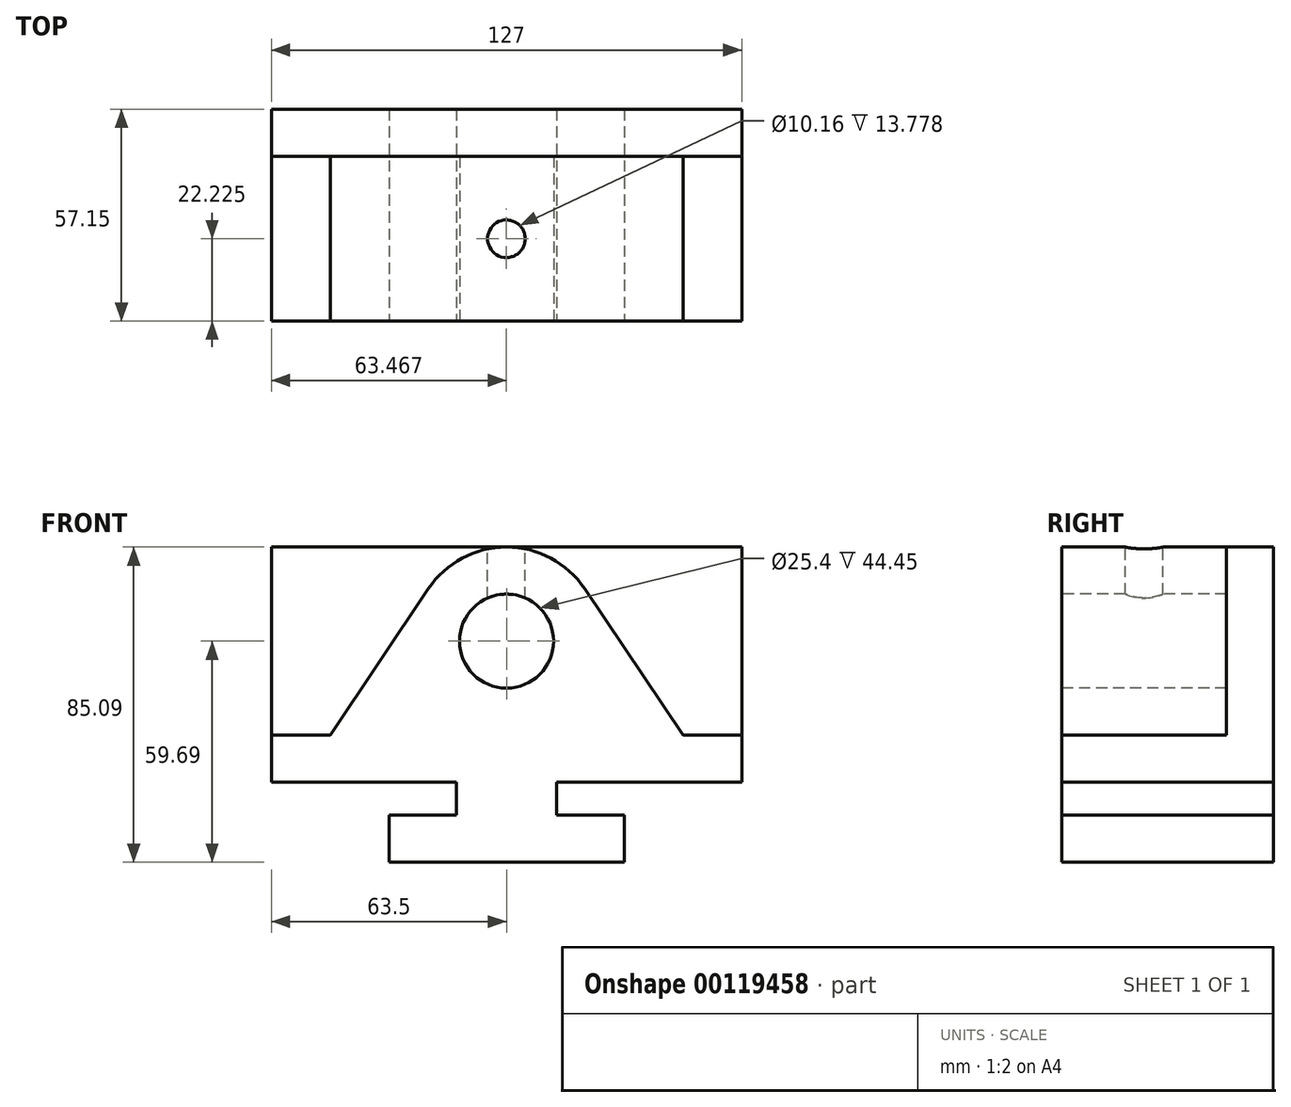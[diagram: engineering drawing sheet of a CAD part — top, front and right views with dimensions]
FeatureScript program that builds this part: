
annotation { "Feature Type Name" : "Feature", "Feature Type Description" : "" }
export const myFeature = defineFeature(function(context is Context, id is Id, definition is map)
    precondition{}
    {
        {
            var Q0;
            Q0=qCreatedBy(makeId("Front.planeOp"),FACE);
            var sketch = newSketch(context, id + "F0", { "sketchPlane" : qUnion([Q0])});
            skPoint(sketch, "E0.middle", {"position": v(0, 0) * mm});
            skLineSegment(sketch, "E1.bottom", {"start": v(31.75, 0) * mm, "end": v(-31.75, 0) * mm});
            skLineSegment(sketch, "E2", {"start": v(-13.47, 12.7) * mm, "end": v(-13.47, 21.6) * mm});
            skLineSegment(sketch, "E3", {"start": v(-13.47, 21.6) * mm, "end": v(-63.5, 21.59) * mm});
            skLineSegment(sketch, "E4", {"start": v(-63.5, 21.59) * mm, "end": v(-63.5, 85.1) * mm});
            skLineSegment(sketch, "E5", {"start": v(-63.5, 85.1) * mm, "end": v(63.5, 85.1) * mm});
            skLineSegment(sketch, "E6", {"start": v(63.5, 85.1) * mm, "end": v(63.5, 21.6) * mm});
            skLineSegment(sketch, "E7", {"start": v(-31.75, 0) * mm, "end": v(-31.75, 12.7) * mm});
            skLineSegment(sketch, "E8", {"start": v(-31.75, 12.7) * mm, "end": v(-13.47, 12.7) * mm});
            skLineSegment(sketch, "E9", {"start": v(0, 28.13) * mm, "end": v(0, -9.7) * mm, "construction": true});
            skLineSegment(sketch, "E10.MirrorCS", {"start": v(13.47, 12.7) * mm, "end": v(13.47, 21.6) * mm});
            skLineSegment(sketch, "E11.MirrorCS", {"start": v(31.75, 12.7) * mm, "end": v(13.47, 12.7) * mm});
            skLineSegment(sketch, "E12.MirrorCS", {"start": v(31.75, 0) * mm, "end": v(31.75, 12.7) * mm});
            skLineSegment(sketch, "E13.MirrorCS", {"start": v(13.47, 21.6) * mm, "end": v(63.5, 21.59) * mm});
            skSolve(sketch);
        }
        {
            var Q0;
            Q0=makeQuery(id+"F0.imprint","IMPRINT",FACE,{"disambiguationData":[TD([[makeQuery(id+"F0.imprint","IMPRINT",EDGE,{"derivedFrom":sQuery(id+"F0.wireOp",EDGE,"E1.bottom")}),-1.0]])]});
            extrude(context, id + "F1", {"entities" : qUnion([Q0]), "oppositeDirection" : true, "depth" : 57.15 * mm});
        }
        {
            var Q0;
            Q0=makeQuery(id+"F1.opExtrude","CAP_FACE",FACE,{"disambiguationData":[OSD([sQuery(id+"F0.wireOp",EDGE,"E1.bottom"),sQuery(id+"F0.wireOp",EDGE,"E2"),sQuery(id+"F0.wireOp",EDGE,"E3"),sQuery(id+"F0.wireOp",EDGE,"E4"),sQuery(id+"F0.wireOp",EDGE,"E5"),sQuery(id+"F0.wireOp",EDGE,"E6"),sQuery(id+"F0.wireOp",EDGE,"E7"),sQuery(id+"F0.wireOp",EDGE,"E8"),sQuery(id+"F0.wireOp",EDGE,"E10.MirrorCS"),sQuery(id+"F0.wireOp",EDGE,"E11.MirrorCS"),sQuery(id+"F0.wireOp",EDGE,"E12.MirrorCS"),sQuery(id+"F0.wireOp",EDGE,"E13.MirrorCS")])],"isStart":true});
            var sketch = newSketch(context, id + "F2", { "sketchPlane" : qUnion([Q0])});
            skLineSegment(sketch, "E14", {"start": v(-63.5, 85.1) * mm, "end": v(63.5, 85.1) * mm});
            skLineSegment(sketch, "E15", {"start": v(63.5, 85.1) * mm, "end": v(63.5, 34.3) * mm});
            skLineSegment(sketch, "E16", {"start": v(63.5, 34.3) * mm, "end": v(47.63, 34.3) * mm});
            skLineSegment(sketch, "E17", {"start": v(0, 0) * mm, "end": v(0, 22.1) * mm, "construction": true});
            skLineSegment(sketch, "E18.MirrorCS", {"start": v(-63.5, 34.3) * mm, "end": v(-47.63, 34.3) * mm});
            skLineSegment(sketch, "E19.MirrorCS", {"start": v(-63.5, 85.1) * mm, "end": v(-63.5, 34.3) * mm});
            skCircle(sketch, "E20", {"center": v(0, 59.7) * mm, "radius": 12.7 * mm});
            skLineSegment(sketch, "E21", {"start": v(-47.62, 34.3) * mm, "end": v(-21.1, 73.84) * mm});
            skLineSegment(sketch, "E22.MirrorCS", {"start": v(47.62, 34.3) * mm, "end": v(21.1, 73.84) * mm});
            skArc(sketch, "E23", {"start": v(-21.1, 73.84) * mm, "mid": v(0, 85.1) * mm, "end": v(21.1, 73.84) * mm});
            skSolve(sketch);
        }
        {
            var Q0;
            Q0=makeQuery(id+"F2.imprint","IMPRINT",FACE,{"disambiguationData":[TD([[makeQuery(id+"F2.imprint","IMPRINT",EDGE,{"derivedFrom":sQuery(id+"F2.wireOp",EDGE,"E18.MirrorCS")}),1.0]])]});
            var Q1;
            Q1=makeQuery(id+"F2.imprint","IMPRINT",FACE,{"disambiguationData":[TD([[makeQuery(id+"F2.imprint","IMPRINT",EDGE,{"derivedFrom":sQuery(id+"F2.wireOp",EDGE,"E20")}),1.0]])]});
            var Q2;
            {var subQ1=sQuery(id+"F2.wireOp",EDGE,"E15");Q2=makeQuery(id+"F2.imprint","IMPRINT",FACE,{"disambiguationData":[TD([[makeQuery(id+"F2.imprint","IMPRINT",EDGE,{"derivedFrom":subQ1}),-1.0]])]});}
            extrude(context, id + "F3", {"entities" : qUnion([Q0, Q1, Q2]), "operationType" : NewBodyOperationType.REMOVE, "oppositeDirection" : true, "depth" : 44.45 * mm});
        }
        {
            var Q0;
            Q0=makeQuery(id+"F1.opExtrude","SWEPT_FACE",FACE,{"disambiguationData":[OSD([sQuery(id+"F0.wireOp",EDGE,"E5")])]});
            var sketch = newSketch(context, id + "F4", { "sketchPlane" : qUnion([Q0])});
            skCircle(sketch, "E24", {"center": v(-0.03, 22.23) * mm, "radius": 5.08 * mm});
            skSolve(sketch);
        }
        {
            var Q0;
            Q0 = qSketchRegion(id + "F4", true);
            extrude(context, id + "F5", {"entities" : qUnion([Q0]), "operationType" : NewBodyOperationType.REMOVE, "endBound" : BoundingType.UP_TO_NEXT, "oppositeDirection" : true, "depth" : 15.24 * mm});
        }
    });
